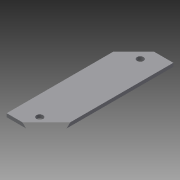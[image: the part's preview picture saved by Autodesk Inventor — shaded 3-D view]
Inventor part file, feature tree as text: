
AUTODESK INVENTOR PART (.ipt)
format: ipt  version: 2015 (Build 190159000, 159)  size: 84,992 bytes
history: native  units: in
note: dims shown in document units (in); Inventor stores cm internally (conversion verified against a paired STEP export)
features: extrude x2, sketch x2, projected_geometry x1
ambient origin geometry x8: Origin, YZ Plane, XZ Plane, XY Plane, X Axis, Y Axis, Z Axis, Center Point
bodies: Solid1 (feature_tree)
feature tree (5):
  extrude  "Extrusion1"  Depth=0.13in
  extrude  "Extrusion2"  Depth=9.3625in
  sketch  "Sketch1"  dims[d0=1.5in d1=0.13in]
  sketch  "Sketch2"  dims[d2=9.3625in d3=0.0in d6=0.25in d7=0.25in d8=4.8in d9=0.0in d10=3.8in]
  projected_geometry  "Projected Loop1"
